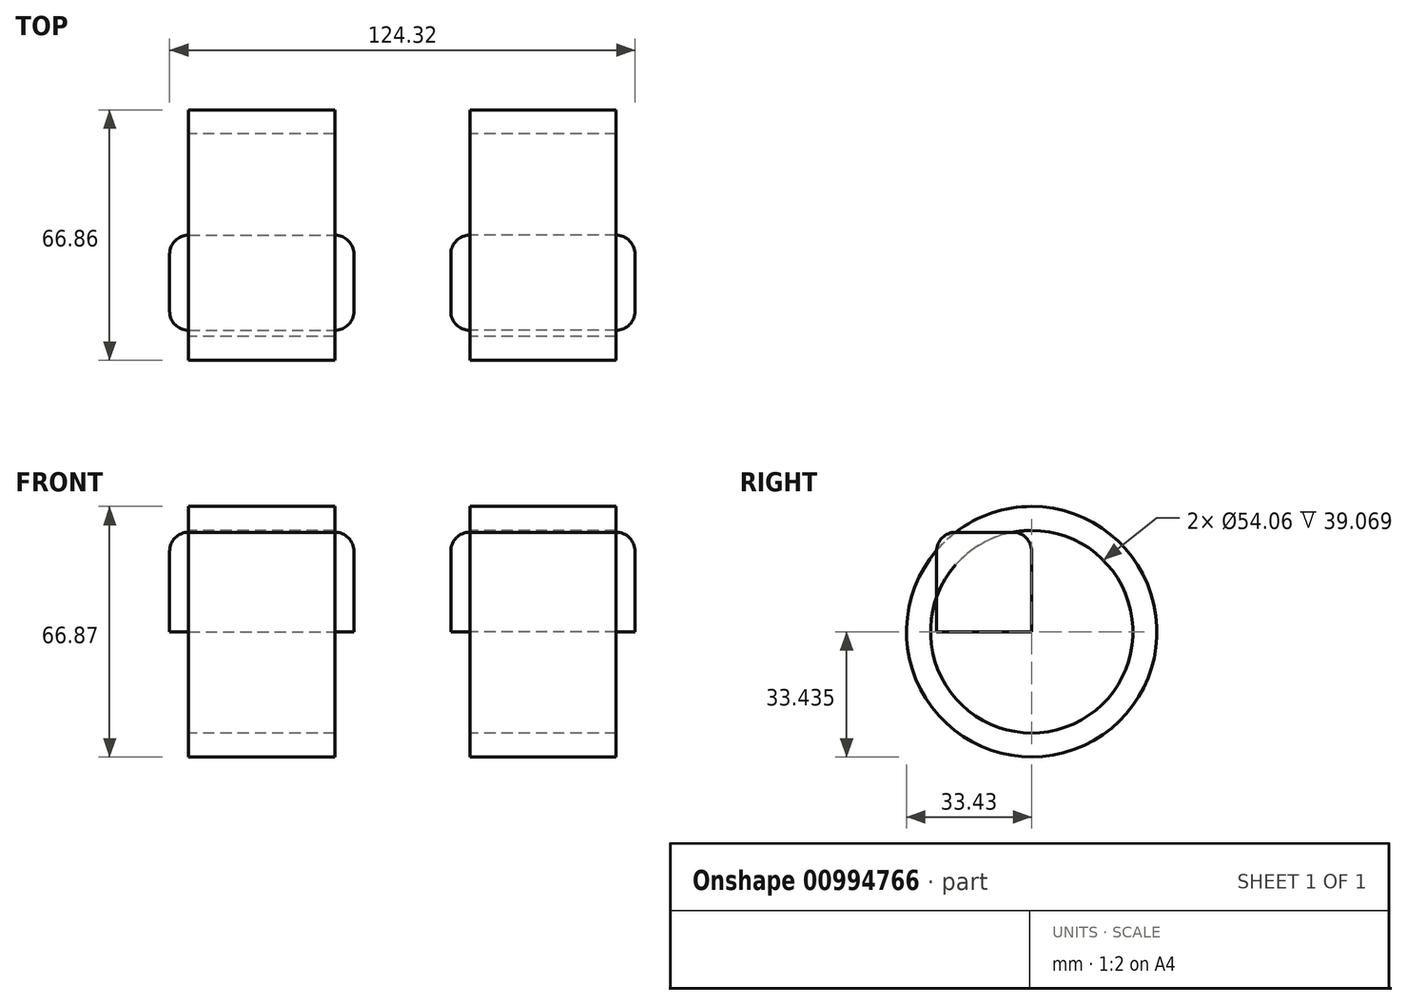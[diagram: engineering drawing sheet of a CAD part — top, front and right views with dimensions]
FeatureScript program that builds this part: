
annotation { "Feature Type Name" : "Feature", "Feature Type Description" : "" }
export const myFeature = defineFeature(function(context is Context, id is Id, definition is map)
    precondition{}
    {
        {
            var Q0;
            Q0=qCreatedBy(makeId("Front.planeOp"),FACE);
            var sketch = newSketch(context, id + "F0", { "sketchPlane" : qUnion([Q0])});
            skLineSegment(sketch, "E0.bottom", {"start": v(-62.16, 20.96) * mm, "end": v(-12.93, 20.96) * mm});
            skLineSegment(sketch, "E0.top", {"start": v(-62.16, -5.59) * mm, "end": v(-12.93, -5.59) * mm});
            skLineSegment(sketch, "E0.left", {"start": v(-62.16, 20.96) * mm, "end": v(-62.16, -5.59) * mm});
            skLineSegment(sketch, "E0.right", {"start": v(-12.93, 20.96) * mm, "end": v(-12.93, -5.59) * mm});
            skSolve(sketch);
        }
        {
            var Q0;
            Q0 = qSketchRegion(id + "F0", true);
            var Q1;
            Q1=makeQuery(id+"F0.imprint","IMPRINT",FACE,{"disambiguationData":[TD([[makeQuery(id+"F0.imprint","IMPRINT",EDGE,{"derivedFrom":sQuery(id+"F0.wireOp",EDGE,"E0.bottom")}),-1.0]])]});
            extrude(context, id + "F1", {"entities" : qUnion([Q0, Q1]), "depth" : 25.4 * mm, "offsetDistance" : 25.4 * mm});
        }
        {
            var Q0;
            Q0=makeQuery(id+"F1.opExtrude","CAP_EDGE",EDGE,{"disambiguationData":[OSD([sQuery(id+"F0.wireOp",EDGE,"E0.bottom")])],"isStart":true});
            var Q1;
            Q1=makeQuery(id+"F1.opExtrude","SWEPT_EDGE",EDGE,{"disambiguationData":[OSD([sQuery(id+"F0.wireOp",EDGE,"E0.bottom"),sQuery(id+"F0.wireOp",EDGE,"E0.right")])]});
            var Q2;
            Q2=makeQuery(id+"F1.opExtrude","CAP_EDGE",EDGE,{"disambiguationData":[OSD([sQuery(id+"F0.wireOp",EDGE,"E0.bottom")])],"isStart":false});
            var Q3;
            Q3=makeQuery(id+"F1.opExtrude","SWEPT_EDGE",EDGE,{"disambiguationData":[OSD([sQuery(id+"F0.wireOp",EDGE,"E0.bottom"),sQuery(id+"F0.wireOp",EDGE,"E0.left")])]});
            var Q4;
            Q4=makeQuery(id+"F1.opExtrude","CAP_EDGE",EDGE,{"disambiguationData":[OSD([sQuery(id+"F0.wireOp",EDGE,"E0.left")])],"isStart":false});
            var Q5;
            Q5=makeQuery(id+"F1.opExtrude","CAP_EDGE",EDGE,{"disambiguationData":[OSD([sQuery(id+"F0.wireOp",EDGE,"E0.right")])],"isStart":false});
            var Q6;
            Q6=makeQuery(id+"F1.opExtrude","CAP_EDGE",EDGE,{"disambiguationData":[OSD([sQuery(id+"F0.wireOp",EDGE,"E0.right")])],"isStart":true});
            var Q7;
            Q7=makeQuery(id+"F1.opExtrude","CAP_EDGE",EDGE,{"disambiguationData":[OSD([sQuery(id+"F0.wireOp",EDGE,"E0.left")])],"isStart":true});
            fillet(context, id + "F2", {"entities" : qUnion([Q0, Q1, Q2, Q3, Q4, Q5, Q6, Q7]), "radius" : 5.08 * mm, "tangentPropagation" : true, "allowEdgeOverflow" : false});
        }
        {
            var Q0;
            Q0=makeQuery(id+"F1.opExtrude","SWEPT_BODY",BODY,{"disambiguationData":[OSD([sQuery(id+"F0.wireOp",EDGE,"E0.bottom"),sQuery(id+"F0.wireOp",EDGE,"E0.top"),sQuery(id+"F0.wireOp",EDGE,"E0.left"),sQuery(id+"F0.wireOp",EDGE,"E0.right")])]});
            var Q1;
            Q1=qCreatedBy(makeId("Right.planeOp"),FACE);
            mirror(context, id + "F3", {"entities" : qUnion([Q0]), "mirrorPlane" : qUnion([Q1])});
        }
        {
            var Q0;
            Q0=makeQuery(id+"F3.opPattern","COPY",FACE,{"derivedFrom":makeQuery(id+"F1.opExtrude","SWEPT_FACE",FACE,{"disambiguationData":[OSD([sQuery(id+"F0.wireOp",EDGE,"E0.bottom")])]}),"instanceName":"1"});
            var Q1;
            Q1=makeQuery(id+"F1.opExtrude","SWEPT_FACE",FACE,{"disambiguationData":[OSD([sQuery(id+"F0.wireOp",EDGE,"E0.bottom")])]});
            var Q2;
            Q2=sQuery(id+"F0.wireOp",EDGE,"E0.top");
            revolve(context, id + "F4", {"surfaceOperationType" : NewSurfaceOperationType.NEW, "entities" : qUnion([Q0, Q1]), "axis" : qUnion([Q2]), "revolveType" : RevolveType.FULL});
        }
    });
